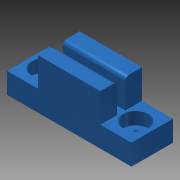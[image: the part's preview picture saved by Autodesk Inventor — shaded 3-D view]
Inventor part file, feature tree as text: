
AUTODESK INVENTOR PART (.ipt)
format: ipt  version: 2013 (Build 170138000, 138)  size: 121,856 bytes
history: native  units: mm
features: extrude x3, sketch x3, fillet x1
ambient origin geometry x8: Origin, YZ Plane, XZ Plane, XY Plane, X Axis, Y Axis, Z Axis, Center Point
bodies: Solid1 (feature_tree)
feature tree (7):
  extrude  "Extrusion1"  Depth=10.0mm
  extrude  "Extrusion2"  Depth=15.0mm
  fillet  "Fillet1"  Radius=15.0mm
  extrude  "Extrusion3"  Depth=3.0mm
  sketch  "Sketch1"  dims[d0=30.0mm d1=10.0mm]
  sketch  "Sketch2"  dims[d4=5.0mm d5=0.0mm d14=15.0mm d15=15.0mm]
  sketch  "Sketch3"  dims[d20=7.0mm d21=0.0mm d22=3.0mm d23=3.0mm d24=4.0mm d25=4.0mm d31=2.0mm d32=4.0mm d33=4.0mm d34=1.0mm d35=6.0mm d36=6.0mm d37=3.0mm d38=0.0mm]
